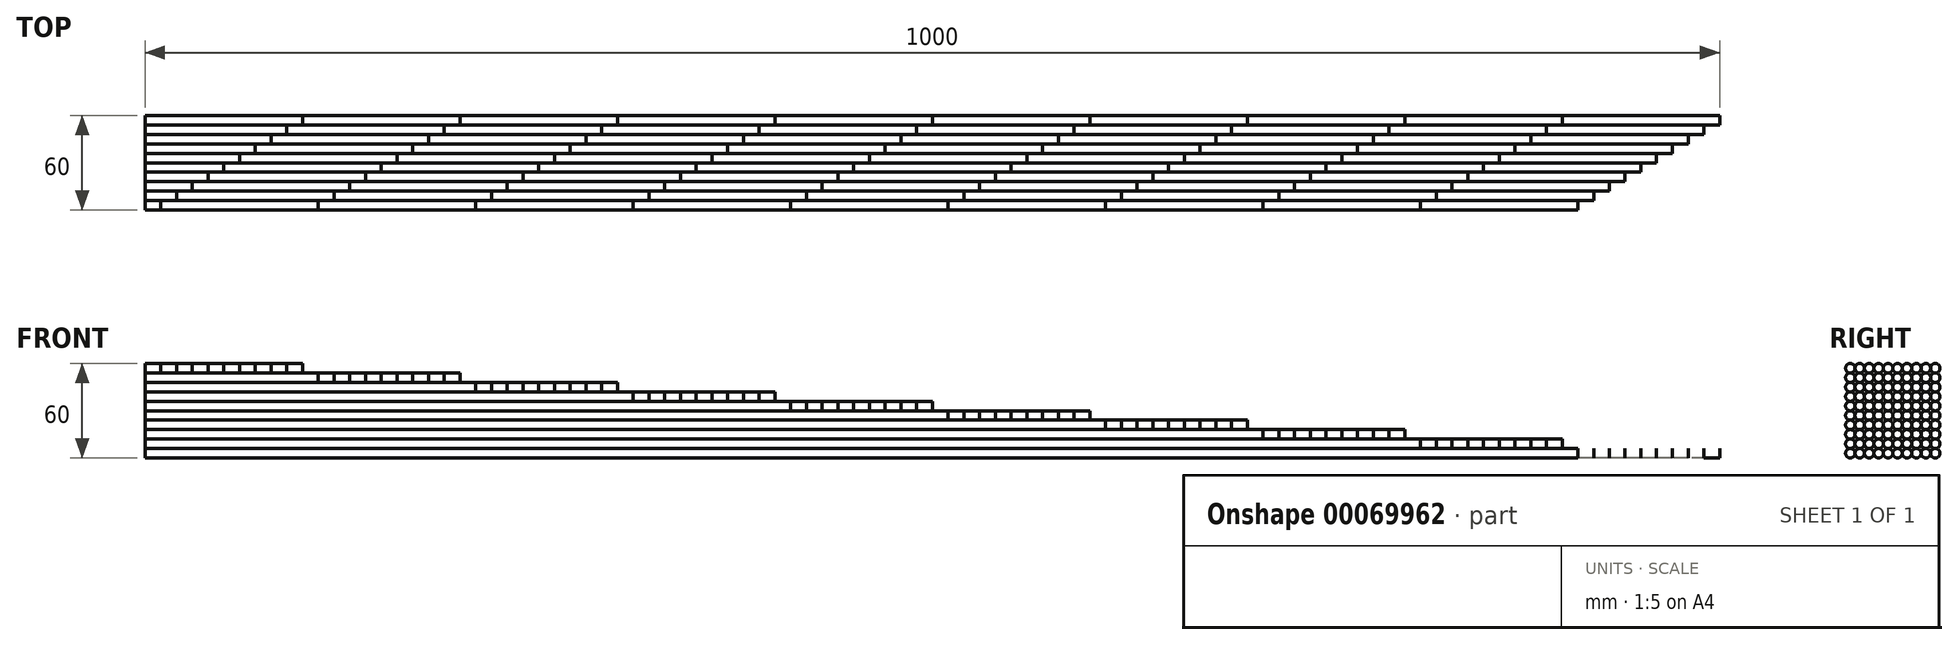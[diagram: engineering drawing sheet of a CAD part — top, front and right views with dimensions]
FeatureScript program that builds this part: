
annotation { "Feature Type Name" : "Feature", "Feature Type Description" : "" }
export const myFeature = defineFeature(function(context is Context, id is Id, definition is map)
    precondition{}
    {
        {
            var Q0;
            Q0=qCreatedBy(makeId("Right.planeOp"),FACE);
            var sketch = newSketch(context, id + "F0", { "sketchPlane" : qUnion([Q0])});
            skCircle(sketch, "E0", {"center": v(0, 0) * mm, "radius": 3 * mm});
            skCircle(sketch, "E1.0.1.0", {"center": v(0, 6) * mm, "radius": 3 * mm});
            skCircle(sketch, "E1.0.2.0", {"center": v(0, 12) * mm, "radius": 3 * mm});
            skCircle(sketch, "E1.0.3.0", {"center": v(0, 18) * mm, "radius": 3 * mm});
            skCircle(sketch, "E1.0.4.0", {"center": v(0, 24) * mm, "radius": 3 * mm});
            skCircle(sketch, "E1.0.5.0", {"center": v(0, 30) * mm, "radius": 3 * mm});
            skCircle(sketch, "E1.0.6.0", {"center": v(0, 36) * mm, "radius": 3 * mm});
            skCircle(sketch, "E1.0.7.0", {"center": v(0, 42) * mm, "radius": 3 * mm});
            skCircle(sketch, "E1.0.8.0", {"center": v(0, 48) * mm, "radius": 3 * mm});
            skCircle(sketch, "E1.0.9.0", {"center": v(0, 54) * mm, "radius": 3 * mm});
            skCircle(sketch, "E1.1.0.0", {"center": v(6, 0) * mm, "radius": 3 * mm});
            skCircle(sketch, "E1.1.1.0", {"center": v(6, 6) * mm, "radius": 3 * mm});
            skCircle(sketch, "E1.1.2.0", {"center": v(6, 12) * mm, "radius": 3 * mm});
            skCircle(sketch, "E1.1.3.0", {"center": v(6, 18) * mm, "radius": 3 * mm});
            skCircle(sketch, "E1.1.4.0", {"center": v(6, 24) * mm, "radius": 3 * mm});
            skCircle(sketch, "E1.1.5.0", {"center": v(6, 30) * mm, "radius": 3 * mm});
            skCircle(sketch, "E1.1.6.0", {"center": v(6, 36) * mm, "radius": 3 * mm});
            skCircle(sketch, "E1.1.7.0", {"center": v(6, 42) * mm, "radius": 3 * mm});
            skCircle(sketch, "E1.1.8.0", {"center": v(6, 48) * mm, "radius": 3 * mm});
            skCircle(sketch, "E1.1.9.0", {"center": v(6, 54) * mm, "radius": 3 * mm});
            skCircle(sketch, "E1.2.0.0", {"center": v(12, 0) * mm, "radius": 3 * mm});
            skCircle(sketch, "E1.2.1.0", {"center": v(12, 6) * mm, "radius": 3 * mm});
            skCircle(sketch, "E1.2.2.0", {"center": v(12, 12) * mm, "radius": 3 * mm});
            skCircle(sketch, "E1.2.3.0", {"center": v(12, 18) * mm, "radius": 3 * mm});
            skCircle(sketch, "E1.2.4.0", {"center": v(12, 24) * mm, "radius": 3 * mm});
            skCircle(sketch, "E1.2.5.0", {"center": v(12, 30) * mm, "radius": 3 * mm});
            skCircle(sketch, "E1.2.6.0", {"center": v(12, 36) * mm, "radius": 3 * mm});
            skCircle(sketch, "E1.2.7.0", {"center": v(12, 42) * mm, "radius": 3 * mm});
            skCircle(sketch, "E1.2.8.0", {"center": v(12, 48) * mm, "radius": 3 * mm});
            skCircle(sketch, "E1.2.9.0", {"center": v(12, 54) * mm, "radius": 3 * mm});
            skCircle(sketch, "E1.3.0.0", {"center": v(18, 0) * mm, "radius": 3 * mm});
            skCircle(sketch, "E1.3.1.0", {"center": v(18, 6) * mm, "radius": 3 * mm});
            skCircle(sketch, "E1.3.2.0", {"center": v(18, 12) * mm, "radius": 3 * mm});
            skCircle(sketch, "E1.3.3.0", {"center": v(18, 18) * mm, "radius": 3 * mm});
            skCircle(sketch, "E1.3.4.0", {"center": v(18, 24) * mm, "radius": 3 * mm});
            skCircle(sketch, "E1.3.5.0", {"center": v(18, 30) * mm, "radius": 3 * mm});
            skCircle(sketch, "E1.3.6.0", {"center": v(18, 36) * mm, "radius": 3 * mm});
            skCircle(sketch, "E1.3.7.0", {"center": v(18, 42) * mm, "radius": 3 * mm});
            skCircle(sketch, "E1.3.8.0", {"center": v(18, 48) * mm, "radius": 3 * mm});
            skCircle(sketch, "E1.3.9.0", {"center": v(18, 54) * mm, "radius": 3 * mm});
            skCircle(sketch, "E1.4.0.0", {"center": v(24, 0) * mm, "radius": 3 * mm});
            skCircle(sketch, "E1.4.1.0", {"center": v(24, 6) * mm, "radius": 3 * mm});
            skCircle(sketch, "E1.4.2.0", {"center": v(24, 12) * mm, "radius": 3 * mm});
            skCircle(sketch, "E1.4.3.0", {"center": v(24, 18) * mm, "radius": 3 * mm});
            skCircle(sketch, "E1.4.4.0", {"center": v(24, 24) * mm, "radius": 3 * mm});
            skCircle(sketch, "E1.4.5.0", {"center": v(24, 30) * mm, "radius": 3 * mm});
            skCircle(sketch, "E1.4.6.0", {"center": v(24, 36) * mm, "radius": 3 * mm});
            skCircle(sketch, "E1.4.7.0", {"center": v(24, 42) * mm, "radius": 3 * mm});
            skCircle(sketch, "E1.4.8.0", {"center": v(24, 48) * mm, "radius": 3 * mm});
            skCircle(sketch, "E1.4.9.0", {"center": v(24, 54) * mm, "radius": 3 * mm});
            skCircle(sketch, "E1.5.0.0", {"center": v(30, 0) * mm, "radius": 3 * mm});
            skCircle(sketch, "E1.5.1.0", {"center": v(30, 6) * mm, "radius": 3 * mm});
            skCircle(sketch, "E1.5.2.0", {"center": v(30, 12) * mm, "radius": 3 * mm});
            skCircle(sketch, "E1.5.3.0", {"center": v(30, 18) * mm, "radius": 3 * mm});
            skCircle(sketch, "E1.5.4.0", {"center": v(30, 24) * mm, "radius": 3 * mm});
            skCircle(sketch, "E1.5.5.0", {"center": v(30, 30) * mm, "radius": 3 * mm});
            skCircle(sketch, "E1.5.6.0", {"center": v(30, 36) * mm, "radius": 3 * mm});
            skCircle(sketch, "E1.5.7.0", {"center": v(30, 42) * mm, "radius": 3 * mm});
            skCircle(sketch, "E1.5.8.0", {"center": v(30, 48) * mm, "radius": 3 * mm});
            skCircle(sketch, "E1.5.9.0", {"center": v(30, 54) * mm, "radius": 3 * mm});
            skCircle(sketch, "E1.6.0.0", {"center": v(36, 0) * mm, "radius": 3 * mm});
            skCircle(sketch, "E1.6.1.0", {"center": v(36, 6) * mm, "radius": 3 * mm});
            skCircle(sketch, "E1.6.2.0", {"center": v(36, 12) * mm, "radius": 3 * mm});
            skCircle(sketch, "E1.6.3.0", {"center": v(36, 18) * mm, "radius": 3 * mm});
            skCircle(sketch, "E1.6.4.0", {"center": v(36, 24) * mm, "radius": 3 * mm});
            skCircle(sketch, "E1.6.5.0", {"center": v(36, 30) * mm, "radius": 3 * mm});
            skCircle(sketch, "E1.6.6.0", {"center": v(36, 36) * mm, "radius": 3 * mm});
            skCircle(sketch, "E1.6.7.0", {"center": v(36, 42) * mm, "radius": 3 * mm});
            skCircle(sketch, "E1.6.8.0", {"center": v(36, 48) * mm, "radius": 3 * mm});
            skCircle(sketch, "E1.6.9.0", {"center": v(36, 54) * mm, "radius": 3 * mm});
            skCircle(sketch, "E1.7.0.0", {"center": v(42, 0) * mm, "radius": 3 * mm});
            skCircle(sketch, "E1.7.1.0", {"center": v(42, 6) * mm, "radius": 3 * mm});
            skCircle(sketch, "E1.7.2.0", {"center": v(42, 12) * mm, "radius": 3 * mm});
            skCircle(sketch, "E1.7.3.0", {"center": v(42, 18) * mm, "radius": 3 * mm});
            skCircle(sketch, "E1.7.4.0", {"center": v(42, 24) * mm, "radius": 3 * mm});
            skCircle(sketch, "E1.7.5.0", {"center": v(42, 30) * mm, "radius": 3 * mm});
            skCircle(sketch, "E1.7.6.0", {"center": v(42, 36) * mm, "radius": 3 * mm});
            skCircle(sketch, "E1.7.7.0", {"center": v(42, 42) * mm, "radius": 3 * mm});
            skCircle(sketch, "E1.7.8.0", {"center": v(42, 48) * mm, "radius": 3 * mm});
            skCircle(sketch, "E1.7.9.0", {"center": v(42, 54) * mm, "radius": 3 * mm});
            skCircle(sketch, "E1.8.0.0", {"center": v(48, 0) * mm, "radius": 3 * mm});
            skCircle(sketch, "E1.8.1.0", {"center": v(48, 6) * mm, "radius": 3 * mm});
            skCircle(sketch, "E1.8.2.0", {"center": v(48, 12) * mm, "radius": 3 * mm});
            skCircle(sketch, "E1.8.3.0", {"center": v(48, 18) * mm, "radius": 3 * mm});
            skCircle(sketch, "E1.8.4.0", {"center": v(48, 24) * mm, "radius": 3 * mm});
            skCircle(sketch, "E1.8.5.0", {"center": v(48, 30) * mm, "radius": 3 * mm});
            skCircle(sketch, "E1.8.6.0", {"center": v(48, 36) * mm, "radius": 3 * mm});
            skCircle(sketch, "E1.8.7.0", {"center": v(48, 42) * mm, "radius": 3 * mm});
            skCircle(sketch, "E1.8.8.0", {"center": v(48, 48) * mm, "radius": 3 * mm});
            skCircle(sketch, "E1.8.9.0", {"center": v(48, 54) * mm, "radius": 3 * mm});
            skCircle(sketch, "E1.9.0.0", {"center": v(54, 0) * mm, "radius": 3 * mm});
            skCircle(sketch, "E1.9.1.0", {"center": v(54, 6) * mm, "radius": 3 * mm});
            skCircle(sketch, "E1.9.2.0", {"center": v(54, 12) * mm, "radius": 3 * mm});
            skCircle(sketch, "E1.9.3.0", {"center": v(54, 18) * mm, "radius": 3 * mm});
            skCircle(sketch, "E1.9.4.0", {"center": v(54, 24) * mm, "radius": 3 * mm});
            skCircle(sketch, "E1.9.5.0", {"center": v(54, 30) * mm, "radius": 3 * mm});
            skCircle(sketch, "E1.9.6.0", {"center": v(54, 36) * mm, "radius": 3 * mm});
            skCircle(sketch, "E1.9.7.0", {"center": v(54, 42) * mm, "radius": 3 * mm});
            skCircle(sketch, "E1.9.8.0", {"center": v(54, 48) * mm, "radius": 3 * mm});
            skCircle(sketch, "E1.9.9.0", {"center": v(54, 54) * mm, "radius": 3 * mm});
            skLineSegment(sketch, "E1.direction1", {"start": v(0, 0) * mm, "end": v(6, 0) * mm, "construction": true});
            skLineSegment(sketch, "E1.direction2", {"start": v(0, 0) * mm, "end": v(0, 6) * mm, "construction": true});
            skSolve(sketch);
        }
        {
            var Q0;
            {var subQ0=sQuery(id+"F0.wireOp",EDGE,"E1.0.9.0");var subQ1=makeQuery(id+"F0.imprint","INTERSECT",VERTEX,{"derivedFrom":[sQuery(id+"F0.wireOp",EDGE,"E1.0.8.0"),subQ0]});Q0=makeQuery(id+"F0.imprint","IMPRINT",FACE,{"disambiguationData":[TD([[makeQuery(id+"F0.imprint","IMPRINT",EDGE,{"disambiguationData":[TD([[subQ1,1.0]])],"derivedFrom":subQ0}),1.0]])]});}
            extrude(context, id + "F1", {"entities" : qUnion([Q0]), "depth" : 10 * mm});
        }
        {
            var Q0;
            {var subQ0=sQuery(id+"F0.wireOp",EDGE,"E1.1.9.0");var subQ1=makeQuery(id+"F0.imprint","INTERSECT",VERTEX,{"derivedFrom":[sQuery(id+"F0.wireOp",EDGE,"E1.0.9.0"),subQ0]});Q0=makeQuery(id+"F0.imprint","IMPRINT",FACE,{"disambiguationData":[TD([[makeQuery(id+"F0.imprint","IMPRINT",EDGE,{"disambiguationData":[TD([[subQ1,1.0]])],"derivedFrom":subQ0}),1.0]])]});}
            extrude(context, id + "F2", {"entities" : qUnion([Q0]), "depth" : 20 * mm});
        }
        {
            var Q0;
            {var subQ0=sQuery(id+"F0.wireOp",EDGE,"E1.2.9.0");var subQ1=makeQuery(id+"F0.imprint","INTERSECT",VERTEX,{"derivedFrom":[sQuery(id+"F0.wireOp",EDGE,"E1.1.9.0"),subQ0]});Q0=makeQuery(id+"F0.imprint","IMPRINT",FACE,{"disambiguationData":[TD([[makeQuery(id+"F0.imprint","IMPRINT",EDGE,{"disambiguationData":[TD([[subQ1,1.0]])],"derivedFrom":subQ0}),1.0]])]});}
            extrude(context, id + "F3", {"entities" : qUnion([Q0]), "depth" : 30 * mm});
        }
        {
            var Q0;
            {var subQ0=sQuery(id+"F0.wireOp",EDGE,"E1.3.9.0");var subQ1=makeQuery(id+"F0.imprint","INTERSECT",VERTEX,{"derivedFrom":[sQuery(id+"F0.wireOp",EDGE,"E1.2.9.0"),subQ0]});Q0=makeQuery(id+"F0.imprint","IMPRINT",FACE,{"disambiguationData":[TD([[makeQuery(id+"F0.imprint","IMPRINT",EDGE,{"disambiguationData":[TD([[subQ1,1.0]])],"derivedFrom":subQ0}),1.0]])]});}
            extrude(context, id + "F4", {"entities" : qUnion([Q0]), "depth" : 40 * mm});
        }
        {
            var Q0;
            {var subQ0=sQuery(id+"F0.wireOp",EDGE,"E1.4.9.0");var subQ1=makeQuery(id+"F0.imprint","INTERSECT",VERTEX,{"derivedFrom":[sQuery(id+"F0.wireOp",EDGE,"E1.3.9.0"),subQ0]});Q0=makeQuery(id+"F0.imprint","IMPRINT",FACE,{"disambiguationData":[TD([[makeQuery(id+"F0.imprint","IMPRINT",EDGE,{"disambiguationData":[TD([[subQ1,1.0]])],"derivedFrom":subQ0}),1.0]])]});}
            extrude(context, id + "F5", {"entities" : qUnion([Q0]), "depth" : 50 * mm});
        }
        {
            var Q0;
            {var subQ0=sQuery(id+"F0.wireOp",EDGE,"E1.5.9.0");var subQ1=makeQuery(id+"F0.imprint","INTERSECT",VERTEX,{"derivedFrom":[sQuery(id+"F0.wireOp",EDGE,"E1.4.9.0"),subQ0]});Q0=makeQuery(id+"F0.imprint","IMPRINT",FACE,{"disambiguationData":[TD([[makeQuery(id+"F0.imprint","IMPRINT",EDGE,{"disambiguationData":[TD([[subQ1,1.0]])],"derivedFrom":subQ0}),1.0]])]});}
            extrude(context, id + "F6", {"entities" : qUnion([Q0]), "depth" : 60 * mm});
        }
        {
            var Q0;
            {var subQ0=sQuery(id+"F0.wireOp",EDGE,"E1.6.9.0");var subQ1=makeQuery(id+"F0.imprint","INTERSECT",VERTEX,{"derivedFrom":[sQuery(id+"F0.wireOp",EDGE,"E1.5.9.0"),subQ0]});Q0=makeQuery(id+"F0.imprint","IMPRINT",FACE,{"disambiguationData":[TD([[makeQuery(id+"F0.imprint","IMPRINT",EDGE,{"disambiguationData":[TD([[subQ1,1.0]])],"derivedFrom":subQ0}),1.0]])]});}
            extrude(context, id + "F7", {"entities" : qUnion([Q0]), "depth" : 70 * mm});
        }
        {
            var Q0;
            {var subQ0=sQuery(id+"F0.wireOp",EDGE,"E1.7.9.0");var subQ1=makeQuery(id+"F0.imprint","INTERSECT",VERTEX,{"derivedFrom":[sQuery(id+"F0.wireOp",EDGE,"E1.6.9.0"),subQ0]});Q0=makeQuery(id+"F0.imprint","IMPRINT",FACE,{"disambiguationData":[TD([[makeQuery(id+"F0.imprint","IMPRINT",EDGE,{"disambiguationData":[TD([[subQ1,1.0]])],"derivedFrom":subQ0}),1.0]])]});}
            extrude(context, id + "F8", {"entities" : qUnion([Q0]), "depth" : 80 * mm});
        }
        {
            var Q0;
            {var subQ0=sQuery(id+"F0.wireOp",EDGE,"E1.8.9.0");var subQ1=makeQuery(id+"F0.imprint","INTERSECT",VERTEX,{"derivedFrom":[sQuery(id+"F0.wireOp",EDGE,"E1.7.9.0"),subQ0]});Q0=makeQuery(id+"F0.imprint","IMPRINT",FACE,{"disambiguationData":[TD([[makeQuery(id+"F0.imprint","IMPRINT",EDGE,{"disambiguationData":[TD([[subQ1,1.0]])],"derivedFrom":subQ0}),1.0]])]});}
            extrude(context, id + "F9", {"entities" : qUnion([Q0]), "depth" : 90 * mm});
        }
        {
            var Q0;
            {var subQ0=sQuery(id+"F0.wireOp",EDGE,"E1.9.9.0");var subQ1=makeQuery(id+"F0.imprint","INTERSECT",VERTEX,{"derivedFrom":[sQuery(id+"F0.wireOp",EDGE,"E1.8.9.0"),subQ0]});Q0=makeQuery(id+"F0.imprint","IMPRINT",FACE,{"disambiguationData":[TD([[makeQuery(id+"F0.imprint","IMPRINT",EDGE,{"disambiguationData":[TD([[subQ1,-1.0]])],"derivedFrom":subQ0}),1.0]])]});}
            extrude(context, id + "F10", {"entities" : qUnion([Q0]), "depth" : 100 * mm});
        }
        {
            var Q0;
            {var subQ0=sQuery(id+"F0.wireOp",EDGE,"E1.0.8.0");var subQ1=makeQuery(id+"F0.imprint","INTERSECT",VERTEX,{"derivedFrom":[subQ0,sQuery(id+"F0.wireOp",EDGE,"E1.0.9.0")]});Q0=makeQuery(id+"F0.imprint","IMPRINT",FACE,{"disambiguationData":[TD([[makeQuery(id+"F0.imprint","IMPRINT",EDGE,{"disambiguationData":[TD([[subQ1,1.0]])],"derivedFrom":subQ0}),1.0]])]});}
            extrude(context, id + "F11", {"entities" : qUnion([Q0]), "depth" : 110 * mm});
        }
        {
            var Q0;
            {var subQ0=sQuery(id+"F0.wireOp",EDGE,"E1.1.8.0");var subQ1=makeQuery(id+"F0.imprint","INTERSECT",VERTEX,{"derivedFrom":[subQ0,sQuery(id+"F0.wireOp",EDGE,"E1.1.9.0")]});Q0=makeQuery(id+"F0.imprint","IMPRINT",FACE,{"disambiguationData":[TD([[makeQuery(id+"F0.imprint","IMPRINT",EDGE,{"disambiguationData":[TD([[subQ1,1.0]])],"derivedFrom":subQ0}),1.0]])]});}
            extrude(context, id + "F12", {"entities" : qUnion([Q0]), "depth" : 120 * mm});
        }
        {
            var Q0;
            {var subQ0=sQuery(id+"F0.wireOp",EDGE,"E1.2.8.0");var subQ1=makeQuery(id+"F0.imprint","INTERSECT",VERTEX,{"derivedFrom":[subQ0,sQuery(id+"F0.wireOp",EDGE,"E1.2.9.0")]});Q0=makeQuery(id+"F0.imprint","IMPRINT",FACE,{"disambiguationData":[TD([[makeQuery(id+"F0.imprint","IMPRINT",EDGE,{"disambiguationData":[TD([[subQ1,1.0]])],"derivedFrom":subQ0}),1.0]])]});}
            extrude(context, id + "F13", {"entities" : qUnion([Q0]), "depth" : 130 * mm});
        }
        {
            var Q0;
            {var subQ0=sQuery(id+"F0.wireOp",EDGE,"E1.3.8.0");var subQ1=makeQuery(id+"F0.imprint","INTERSECT",VERTEX,{"derivedFrom":[subQ0,sQuery(id+"F0.wireOp",EDGE,"E1.3.9.0")]});Q0=makeQuery(id+"F0.imprint","IMPRINT",FACE,{"disambiguationData":[TD([[makeQuery(id+"F0.imprint","IMPRINT",EDGE,{"disambiguationData":[TD([[subQ1,1.0]])],"derivedFrom":subQ0}),1.0]])]});}
            extrude(context, id + "F14", {"entities" : qUnion([Q0]), "depth" : 140 * mm});
        }
        {
            var Q0;
            {var subQ0=sQuery(id+"F0.wireOp",EDGE,"E1.4.8.0");var subQ1=makeQuery(id+"F0.imprint","INTERSECT",VERTEX,{"derivedFrom":[subQ0,sQuery(id+"F0.wireOp",EDGE,"E1.4.9.0")]});Q0=makeQuery(id+"F0.imprint","IMPRINT",FACE,{"disambiguationData":[TD([[makeQuery(id+"F0.imprint","IMPRINT",EDGE,{"disambiguationData":[TD([[subQ1,1.0]])],"derivedFrom":subQ0}),1.0]])]});}
            extrude(context, id + "F15", {"entities" : qUnion([Q0]), "depth" : 150 * mm});
        }
        {
            var Q0;
            {var subQ0=sQuery(id+"F0.wireOp",EDGE,"E1.5.8.0");var subQ1=makeQuery(id+"F0.imprint","INTERSECT",VERTEX,{"derivedFrom":[subQ0,sQuery(id+"F0.wireOp",EDGE,"E1.5.9.0")]});Q0=makeQuery(id+"F0.imprint","IMPRINT",FACE,{"disambiguationData":[TD([[makeQuery(id+"F0.imprint","IMPRINT",EDGE,{"disambiguationData":[TD([[subQ1,1.0]])],"derivedFrom":subQ0}),1.0]])]});}
            extrude(context, id + "F16", {"entities" : qUnion([Q0]), "depth" : 160 * mm});
        }
        {
            var Q0;
            {var subQ0=sQuery(id+"F0.wireOp",EDGE,"E1.6.8.0");var subQ1=makeQuery(id+"F0.imprint","INTERSECT",VERTEX,{"derivedFrom":[subQ0,sQuery(id+"F0.wireOp",EDGE,"E1.6.9.0")]});Q0=makeQuery(id+"F0.imprint","IMPRINT",FACE,{"disambiguationData":[TD([[makeQuery(id+"F0.imprint","IMPRINT",EDGE,{"disambiguationData":[TD([[subQ1,1.0]])],"derivedFrom":subQ0}),1.0]])]});}
            extrude(context, id + "F17", {"entities" : qUnion([Q0]), "depth" : 170 * mm});
        }
        {
            var Q0;
            {var subQ0=sQuery(id+"F0.wireOp",EDGE,"E1.7.8.0");var subQ1=makeQuery(id+"F0.imprint","INTERSECT",VERTEX,{"derivedFrom":[subQ0,sQuery(id+"F0.wireOp",EDGE,"E1.7.9.0")]});Q0=makeQuery(id+"F0.imprint","IMPRINT",FACE,{"disambiguationData":[TD([[makeQuery(id+"F0.imprint","IMPRINT",EDGE,{"disambiguationData":[TD([[subQ1,1.0]])],"derivedFrom":subQ0}),1.0]])]});}
            extrude(context, id + "F18", {"entities" : qUnion([Q0]), "depth" : 180 * mm});
        }
        {
            var Q0;
            {var subQ0=sQuery(id+"F0.wireOp",EDGE,"E1.8.8.0");var subQ1=makeQuery(id+"F0.imprint","INTERSECT",VERTEX,{"derivedFrom":[subQ0,sQuery(id+"F0.wireOp",EDGE,"E1.8.9.0")]});Q0=makeQuery(id+"F0.imprint","IMPRINT",FACE,{"disambiguationData":[TD([[makeQuery(id+"F0.imprint","IMPRINT",EDGE,{"disambiguationData":[TD([[subQ1,1.0]])],"derivedFrom":subQ0}),1.0]])]});}
            extrude(context, id + "F19", {"entities" : qUnion([Q0]), "depth" : 190 * mm});
        }
        {
            var Q0;
            {var subQ0=sQuery(id+"F0.wireOp",EDGE,"E1.9.8.0");var subQ1=makeQuery(id+"F0.imprint","INTERSECT",VERTEX,{"derivedFrom":[subQ0,sQuery(id+"F0.wireOp",EDGE,"E1.9.9.0")]});Q0=makeQuery(id+"F0.imprint","IMPRINT",FACE,{"disambiguationData":[TD([[makeQuery(id+"F0.imprint","IMPRINT",EDGE,{"disambiguationData":[TD([[subQ1,-1.0]])],"derivedFrom":subQ0}),1.0]])]});}
            extrude(context, id + "F20", {"entities" : qUnion([Q0]), "depth" : 200 * mm});
        }
        {
            var Q0;
            {var subQ0=sQuery(id+"F0.wireOp",EDGE,"E1.0.7.0");var subQ1=makeQuery(id+"F0.imprint","INTERSECT",VERTEX,{"derivedFrom":[subQ0,sQuery(id+"F0.wireOp",EDGE,"E1.0.8.0")]});Q0=makeQuery(id+"F0.imprint","IMPRINT",FACE,{"disambiguationData":[TD([[makeQuery(id+"F0.imprint","IMPRINT",EDGE,{"disambiguationData":[TD([[subQ1,1.0]])],"derivedFrom":subQ0}),1.0]])]});}
            extrude(context, id + "F21", {"entities" : qUnion([Q0]), "depth" : 210 * mm});
        }
        {
            var Q0;
            {var subQ0=sQuery(id+"F0.wireOp",EDGE,"E1.1.7.0");var subQ1=makeQuery(id+"F0.imprint","INTERSECT",VERTEX,{"derivedFrom":[subQ0,sQuery(id+"F0.wireOp",EDGE,"E1.1.8.0")]});Q0=makeQuery(id+"F0.imprint","IMPRINT",FACE,{"disambiguationData":[TD([[makeQuery(id+"F0.imprint","IMPRINT",EDGE,{"disambiguationData":[TD([[subQ1,1.0]])],"derivedFrom":subQ0}),1.0]])]});}
            extrude(context, id + "F22", {"entities" : qUnion([Q0]), "depth" : 220 * mm});
        }
        {
            var Q0;
            {var subQ0=sQuery(id+"F0.wireOp",EDGE,"E1.2.7.0");var subQ1=makeQuery(id+"F0.imprint","INTERSECT",VERTEX,{"derivedFrom":[subQ0,sQuery(id+"F0.wireOp",EDGE,"E1.2.8.0")]});Q0=makeQuery(id+"F0.imprint","IMPRINT",FACE,{"disambiguationData":[TD([[makeQuery(id+"F0.imprint","IMPRINT",EDGE,{"disambiguationData":[TD([[subQ1,1.0]])],"derivedFrom":subQ0}),1.0]])]});}
            extrude(context, id + "F23", {"entities" : qUnion([Q0]), "depth" : 230 * mm});
        }
        {
            var Q0;
            {var subQ0=sQuery(id+"F0.wireOp",EDGE,"E1.3.7.0");var subQ1=makeQuery(id+"F0.imprint","INTERSECT",VERTEX,{"derivedFrom":[subQ0,sQuery(id+"F0.wireOp",EDGE,"E1.3.8.0")]});Q0=makeQuery(id+"F0.imprint","IMPRINT",FACE,{"disambiguationData":[TD([[makeQuery(id+"F0.imprint","IMPRINT",EDGE,{"disambiguationData":[TD([[subQ1,1.0]])],"derivedFrom":subQ0}),1.0]])]});}
            var Q1;
            Q1=sQuery(id+"F0.wireOp",EDGE,"E1.3.7.0");
            extrude(context, id + "F24", {"entities" : qUnion([Q0]), "surfaceEntities" : qUnion([Q1]), "depth" : 240 * mm});
        }
        {
            var Q0;
            {var subQ0=sQuery(id+"F0.wireOp",EDGE,"E1.4.7.0");var subQ1=makeQuery(id+"F0.imprint","INTERSECT",VERTEX,{"derivedFrom":[subQ0,sQuery(id+"F0.wireOp",EDGE,"E1.4.8.0")]});Q0=makeQuery(id+"F0.imprint","IMPRINT",FACE,{"disambiguationData":[TD([[makeQuery(id+"F0.imprint","IMPRINT",EDGE,{"disambiguationData":[TD([[subQ1,1.0]])],"derivedFrom":subQ0}),1.0]])]});}
            extrude(context, id + "F25", {"entities" : qUnion([Q0]), "depth" : 250 * mm});
        }
        {
            var Q0;
            {var subQ0=sQuery(id+"F0.wireOp",EDGE,"E1.5.7.0");var subQ1=makeQuery(id+"F0.imprint","INTERSECT",VERTEX,{"derivedFrom":[subQ0,sQuery(id+"F0.wireOp",EDGE,"E1.5.8.0")]});Q0=makeQuery(id+"F0.imprint","IMPRINT",FACE,{"disambiguationData":[TD([[makeQuery(id+"F0.imprint","IMPRINT",EDGE,{"disambiguationData":[TD([[subQ1,1.0]])],"derivedFrom":subQ0}),1.0]])]});}
            extrude(context, id + "F26", {"entities" : qUnion([Q0]), "depth" : 260 * mm});
        }
        {
            var Q0;
            {var subQ0=sQuery(id+"F0.wireOp",EDGE,"E1.6.7.0");var subQ1=makeQuery(id+"F0.imprint","INTERSECT",VERTEX,{"derivedFrom":[subQ0,sQuery(id+"F0.wireOp",EDGE,"E1.6.8.0")]});Q0=makeQuery(id+"F0.imprint","IMPRINT",FACE,{"disambiguationData":[TD([[makeQuery(id+"F0.imprint","IMPRINT",EDGE,{"disambiguationData":[TD([[subQ1,1.0]])],"derivedFrom":subQ0}),1.0]])]});}
            extrude(context, id + "F27", {"entities" : qUnion([Q0]), "depth" : 270 * mm});
        }
        {
            var Q0;
            {var subQ0=sQuery(id+"F0.wireOp",EDGE,"E1.7.7.0");var subQ1=makeQuery(id+"F0.imprint","INTERSECT",VERTEX,{"derivedFrom":[subQ0,sQuery(id+"F0.wireOp",EDGE,"E1.7.8.0")]});Q0=makeQuery(id+"F0.imprint","IMPRINT",FACE,{"disambiguationData":[TD([[makeQuery(id+"F0.imprint","IMPRINT",EDGE,{"disambiguationData":[TD([[subQ1,1.0]])],"derivedFrom":subQ0}),1.0]])]});}
            extrude(context, id + "F28", {"entities" : qUnion([Q0]), "depth" : 280 * mm});
        }
        {
            var Q0;
            {var subQ0=sQuery(id+"F0.wireOp",EDGE,"E1.8.7.0");var subQ1=makeQuery(id+"F0.imprint","INTERSECT",VERTEX,{"derivedFrom":[subQ0,sQuery(id+"F0.wireOp",EDGE,"E1.8.8.0")]});Q0=makeQuery(id+"F0.imprint","IMPRINT",FACE,{"disambiguationData":[TD([[makeQuery(id+"F0.imprint","IMPRINT",EDGE,{"disambiguationData":[TD([[subQ1,1.0]])],"derivedFrom":subQ0}),1.0]])]});}
            extrude(context, id + "F29", {"entities" : qUnion([Q0]), "depth" : 290 * mm});
        }
        {
            var Q0;
            {var subQ0=sQuery(id+"F0.wireOp",EDGE,"E1.9.7.0");var subQ1=makeQuery(id+"F0.imprint","INTERSECT",VERTEX,{"derivedFrom":[subQ0,sQuery(id+"F0.wireOp",EDGE,"E1.9.8.0")]});Q0=makeQuery(id+"F0.imprint","IMPRINT",FACE,{"disambiguationData":[TD([[makeQuery(id+"F0.imprint","IMPRINT",EDGE,{"disambiguationData":[TD([[subQ1,-1.0]])],"derivedFrom":subQ0}),1.0]])]});}
            extrude(context, id + "F30", {"entities" : qUnion([Q0]), "depth" : 300 * mm});
        }
        {
            var Q0;
            {var subQ0=sQuery(id+"F0.wireOp",EDGE,"E1.0.6.0");var subQ1=makeQuery(id+"F0.imprint","INTERSECT",VERTEX,{"derivedFrom":[subQ0,sQuery(id+"F0.wireOp",EDGE,"E1.0.7.0")]});Q0=makeQuery(id+"F0.imprint","IMPRINT",FACE,{"disambiguationData":[TD([[makeQuery(id+"F0.imprint","IMPRINT",EDGE,{"disambiguationData":[TD([[subQ1,1.0]])],"derivedFrom":subQ0}),1.0]])]});}
            extrude(context, id + "F31", {"entities" : qUnion([Q0]), "depth" : 310 * mm});
        }
        {
            var Q0;
            {var subQ0=sQuery(id+"F0.wireOp",EDGE,"E1.1.6.0");var subQ1=makeQuery(id+"F0.imprint","INTERSECT",VERTEX,{"derivedFrom":[subQ0,sQuery(id+"F0.wireOp",EDGE,"E1.1.7.0")]});Q0=makeQuery(id+"F0.imprint","IMPRINT",FACE,{"disambiguationData":[TD([[makeQuery(id+"F0.imprint","IMPRINT",EDGE,{"disambiguationData":[TD([[subQ1,1.0]])],"derivedFrom":subQ0}),1.0]])]});}
            extrude(context, id + "F32", {"entities" : qUnion([Q0]), "depth" : 320 * mm});
        }
        {
            var Q0;
            {var subQ0=sQuery(id+"F0.wireOp",EDGE,"E1.2.6.0");var subQ1=makeQuery(id+"F0.imprint","INTERSECT",VERTEX,{"derivedFrom":[subQ0,sQuery(id+"F0.wireOp",EDGE,"E1.2.7.0")]});Q0=makeQuery(id+"F0.imprint","IMPRINT",FACE,{"disambiguationData":[TD([[makeQuery(id+"F0.imprint","IMPRINT",EDGE,{"disambiguationData":[TD([[subQ1,1.0]])],"derivedFrom":subQ0}),1.0]])]});}
            extrude(context, id + "F33", {"entities" : qUnion([Q0]), "depth" : 330 * mm});
        }
        {
            var Q0;
            {var subQ0=sQuery(id+"F0.wireOp",EDGE,"E1.3.6.0");var subQ1=makeQuery(id+"F0.imprint","INTERSECT",VERTEX,{"derivedFrom":[subQ0,sQuery(id+"F0.wireOp",EDGE,"E1.3.7.0")]});Q0=makeQuery(id+"F0.imprint","IMPRINT",FACE,{"disambiguationData":[TD([[makeQuery(id+"F0.imprint","IMPRINT",EDGE,{"disambiguationData":[TD([[subQ1,1.0]])],"derivedFrom":subQ0}),1.0]])]});}
            extrude(context, id + "F34", {"entities" : qUnion([Q0]), "depth" : 340 * mm});
        }
        {
            var Q0;
            {var subQ0=sQuery(id+"F0.wireOp",EDGE,"E1.4.6.0");var subQ1=makeQuery(id+"F0.imprint","INTERSECT",VERTEX,{"derivedFrom":[subQ0,sQuery(id+"F0.wireOp",EDGE,"E1.4.7.0")]});Q0=makeQuery(id+"F0.imprint","IMPRINT",FACE,{"disambiguationData":[TD([[makeQuery(id+"F0.imprint","IMPRINT",EDGE,{"disambiguationData":[TD([[subQ1,1.0]])],"derivedFrom":subQ0}),1.0]])]});}
            extrude(context, id + "F35", {"entities" : qUnion([Q0]), "depth" : 350 * mm});
        }
        {
            var Q0;
            {var subQ0=sQuery(id+"F0.wireOp",EDGE,"E1.5.6.0");var subQ1=makeQuery(id+"F0.imprint","INTERSECT",VERTEX,{"derivedFrom":[subQ0,sQuery(id+"F0.wireOp",EDGE,"E1.5.7.0")]});Q0=makeQuery(id+"F0.imprint","IMPRINT",FACE,{"disambiguationData":[TD([[makeQuery(id+"F0.imprint","IMPRINT",EDGE,{"disambiguationData":[TD([[subQ1,1.0]])],"derivedFrom":subQ0}),1.0]])]});}
            extrude(context, id + "F36", {"entities" : qUnion([Q0]), "depth" : 360 * mm});
        }
        {
            var Q0;
            {var subQ0=sQuery(id+"F0.wireOp",EDGE,"E1.6.6.0");var subQ1=makeQuery(id+"F0.imprint","INTERSECT",VERTEX,{"derivedFrom":[subQ0,sQuery(id+"F0.wireOp",EDGE,"E1.6.7.0")]});Q0=makeQuery(id+"F0.imprint","IMPRINT",FACE,{"disambiguationData":[TD([[makeQuery(id+"F0.imprint","IMPRINT",EDGE,{"disambiguationData":[TD([[subQ1,1.0]])],"derivedFrom":subQ0}),1.0]])]});}
            extrude(context, id + "F37", {"entities" : qUnion([Q0]), "depth" : 370 * mm});
        }
        {
            var Q0;
            {var subQ0=sQuery(id+"F0.wireOp",EDGE,"E1.7.6.0");var subQ1=makeQuery(id+"F0.imprint","INTERSECT",VERTEX,{"derivedFrom":[subQ0,sQuery(id+"F0.wireOp",EDGE,"E1.7.7.0")]});Q0=makeQuery(id+"F0.imprint","IMPRINT",FACE,{"disambiguationData":[TD([[makeQuery(id+"F0.imprint","IMPRINT",EDGE,{"disambiguationData":[TD([[subQ1,1.0]])],"derivedFrom":subQ0}),1.0]])]});}
            var Q1;
            Q1=sQuery(id+"F0.wireOp",EDGE,"E1.7.6.0");
            extrude(context, id + "F38", {"entities" : qUnion([Q0]), "surfaceEntities" : qUnion([Q1]), "depth" : 380 * mm});
        }
        {
            var Q0;
            {var subQ0=sQuery(id+"F0.wireOp",EDGE,"E1.8.6.0");var subQ1=makeQuery(id+"F0.imprint","INTERSECT",VERTEX,{"derivedFrom":[subQ0,sQuery(id+"F0.wireOp",EDGE,"E1.8.7.0")]});Q0=makeQuery(id+"F0.imprint","IMPRINT",FACE,{"disambiguationData":[TD([[makeQuery(id+"F0.imprint","IMPRINT",EDGE,{"disambiguationData":[TD([[subQ1,1.0]])],"derivedFrom":subQ0}),1.0]])]});}
            extrude(context, id + "F39", {"entities" : qUnion([Q0]), "depth" : 390 * mm});
        }
        {
            var Q0;
            {var subQ0=sQuery(id+"F0.wireOp",EDGE,"E1.9.6.0");var subQ1=makeQuery(id+"F0.imprint","INTERSECT",VERTEX,{"derivedFrom":[subQ0,sQuery(id+"F0.wireOp",EDGE,"E1.9.7.0")]});Q0=makeQuery(id+"F0.imprint","IMPRINT",FACE,{"disambiguationData":[TD([[makeQuery(id+"F0.imprint","IMPRINT",EDGE,{"disambiguationData":[TD([[subQ1,-1.0]])],"derivedFrom":subQ0}),1.0]])]});}
            extrude(context, id + "F40", {"entities" : qUnion([Q0]), "depth" : 400 * mm});
        }
        {
            var Q0;
            {var subQ0=sQuery(id+"F0.wireOp",EDGE,"E1.0.5.0");var subQ1=makeQuery(id+"F0.imprint","INTERSECT",VERTEX,{"derivedFrom":[subQ0,sQuery(id+"F0.wireOp",EDGE,"E1.0.6.0")]});Q0=makeQuery(id+"F0.imprint","IMPRINT",FACE,{"disambiguationData":[TD([[makeQuery(id+"F0.imprint","IMPRINT",EDGE,{"disambiguationData":[TD([[subQ1,1.0]])],"derivedFrom":subQ0}),1.0]])]});}
            extrude(context, id + "F41", {"entities" : qUnion([Q0]), "depth" : 410 * mm});
        }
        {
            var Q0;
            {var subQ0=sQuery(id+"F0.wireOp",EDGE,"E1.1.5.0");var subQ1=makeQuery(id+"F0.imprint","INTERSECT",VERTEX,{"derivedFrom":[subQ0,sQuery(id+"F0.wireOp",EDGE,"E1.1.6.0")]});Q0=makeQuery(id+"F0.imprint","IMPRINT",FACE,{"disambiguationData":[TD([[makeQuery(id+"F0.imprint","IMPRINT",EDGE,{"disambiguationData":[TD([[subQ1,1.0]])],"derivedFrom":subQ0}),1.0]])]});}
            extrude(context, id + "F42", {"entities" : qUnion([Q0]), "depth" : 420 * mm});
        }
        {
            var Q0;
            {var subQ0=sQuery(id+"F0.wireOp",EDGE,"E1.2.5.0");var subQ1=makeQuery(id+"F0.imprint","INTERSECT",VERTEX,{"derivedFrom":[subQ0,sQuery(id+"F0.wireOp",EDGE,"E1.2.6.0")]});Q0=makeQuery(id+"F0.imprint","IMPRINT",FACE,{"disambiguationData":[TD([[makeQuery(id+"F0.imprint","IMPRINT",EDGE,{"disambiguationData":[TD([[subQ1,1.0]])],"derivedFrom":subQ0}),1.0]])]});}
            extrude(context, id + "F43", {"entities" : qUnion([Q0]), "depth" : 430 * mm});
        }
        {
            var Q0;
            {var subQ0=sQuery(id+"F0.wireOp",EDGE,"E1.3.5.0");var subQ1=makeQuery(id+"F0.imprint","INTERSECT",VERTEX,{"derivedFrom":[subQ0,sQuery(id+"F0.wireOp",EDGE,"E1.3.6.0")]});Q0=makeQuery(id+"F0.imprint","IMPRINT",FACE,{"disambiguationData":[TD([[makeQuery(id+"F0.imprint","IMPRINT",EDGE,{"disambiguationData":[TD([[subQ1,1.0]])],"derivedFrom":subQ0}),1.0]])]});}
            extrude(context, id + "F44", {"entities" : qUnion([Q0]), "depth" : 440 * mm});
        }
        {
            var Q0;
            {var subQ0=sQuery(id+"F0.wireOp",EDGE,"E1.4.5.0");var subQ1=makeQuery(id+"F0.imprint","INTERSECT",VERTEX,{"derivedFrom":[subQ0,sQuery(id+"F0.wireOp",EDGE,"E1.4.6.0")]});Q0=makeQuery(id+"F0.imprint","IMPRINT",FACE,{"disambiguationData":[TD([[makeQuery(id+"F0.imprint","IMPRINT",EDGE,{"disambiguationData":[TD([[subQ1,1.0]])],"derivedFrom":subQ0}),1.0]])]});}
            extrude(context, id + "F45", {"entities" : qUnion([Q0]), "depth" : 450 * mm});
        }
        {
            var Q0;
            {var subQ0=sQuery(id+"F0.wireOp",EDGE,"E1.5.5.0");var subQ1=makeQuery(id+"F0.imprint","INTERSECT",VERTEX,{"derivedFrom":[subQ0,sQuery(id+"F0.wireOp",EDGE,"E1.5.6.0")]});Q0=makeQuery(id+"F0.imprint","IMPRINT",FACE,{"disambiguationData":[TD([[makeQuery(id+"F0.imprint","IMPRINT",EDGE,{"disambiguationData":[TD([[subQ1,1.0]])],"derivedFrom":subQ0}),1.0]])]});}
            extrude(context, id + "F46", {"entities" : qUnion([Q0]), "depth" : 460 * mm});
        }
        {
            var Q0;
            {var subQ0=sQuery(id+"F0.wireOp",EDGE,"E1.6.5.0");var subQ1=makeQuery(id+"F0.imprint","INTERSECT",VERTEX,{"derivedFrom":[subQ0,sQuery(id+"F0.wireOp",EDGE,"E1.6.6.0")]});Q0=makeQuery(id+"F0.imprint","IMPRINT",FACE,{"disambiguationData":[TD([[makeQuery(id+"F0.imprint","IMPRINT",EDGE,{"disambiguationData":[TD([[subQ1,1.0]])],"derivedFrom":subQ0}),1.0]])]});}
            extrude(context, id + "F47", {"entities" : qUnion([Q0]), "depth" : 470 * mm});
        }
        {
            var Q0;
            {var subQ0=sQuery(id+"F0.wireOp",EDGE,"E1.7.5.0");var subQ1=makeQuery(id+"F0.imprint","INTERSECT",VERTEX,{"derivedFrom":[subQ0,sQuery(id+"F0.wireOp",EDGE,"E1.7.6.0")]});Q0=makeQuery(id+"F0.imprint","IMPRINT",FACE,{"disambiguationData":[TD([[makeQuery(id+"F0.imprint","IMPRINT",EDGE,{"disambiguationData":[TD([[subQ1,1.0]])],"derivedFrom":subQ0}),1.0]])]});}
            extrude(context, id + "F48", {"entities" : qUnion([Q0]), "depth" : 480 * mm});
        }
        {
            var Q0;
            {var subQ0=sQuery(id+"F0.wireOp",EDGE,"E1.8.5.0");var subQ1=makeQuery(id+"F0.imprint","INTERSECT",VERTEX,{"derivedFrom":[subQ0,sQuery(id+"F0.wireOp",EDGE,"E1.8.6.0")]});Q0=makeQuery(id+"F0.imprint","IMPRINT",FACE,{"disambiguationData":[TD([[makeQuery(id+"F0.imprint","IMPRINT",EDGE,{"disambiguationData":[TD([[subQ1,1.0]])],"derivedFrom":subQ0}),1.0]])]});}
            extrude(context, id + "F49", {"entities" : qUnion([Q0]), "depth" : 490 * mm});
        }
        {
            var Q0;
            {var subQ0=sQuery(id+"F0.wireOp",EDGE,"E1.9.5.0");var subQ1=makeQuery(id+"F0.imprint","INTERSECT",VERTEX,{"derivedFrom":[subQ0,sQuery(id+"F0.wireOp",EDGE,"E1.9.6.0")]});Q0=makeQuery(id+"F0.imprint","IMPRINT",FACE,{"disambiguationData":[TD([[makeQuery(id+"F0.imprint","IMPRINT",EDGE,{"disambiguationData":[TD([[subQ1,-1.0]])],"derivedFrom":subQ0}),1.0]])]});}
            extrude(context, id + "F50", {"entities" : qUnion([Q0]), "depth" : 500 * mm});
        }
        {
            var Q0;
            {var subQ0=sQuery(id+"F0.wireOp",EDGE,"E1.0.4.0");var subQ1=makeQuery(id+"F0.imprint","INTERSECT",VERTEX,{"derivedFrom":[subQ0,sQuery(id+"F0.wireOp",EDGE,"E1.0.5.0")]});Q0=makeQuery(id+"F0.imprint","IMPRINT",FACE,{"disambiguationData":[TD([[makeQuery(id+"F0.imprint","IMPRINT",EDGE,{"disambiguationData":[TD([[subQ1,1.0]])],"derivedFrom":subQ0}),1.0]])]});}
            extrude(context, id + "F51", {"entities" : qUnion([Q0]), "depth" : 510 * mm});
        }
        {
            var Q0;
            {var subQ0=sQuery(id+"F0.wireOp",EDGE,"E1.1.4.0");var subQ1=makeQuery(id+"F0.imprint","INTERSECT",VERTEX,{"derivedFrom":[subQ0,sQuery(id+"F0.wireOp",EDGE,"E1.1.5.0")]});Q0=makeQuery(id+"F0.imprint","IMPRINT",FACE,{"disambiguationData":[TD([[makeQuery(id+"F0.imprint","IMPRINT",EDGE,{"disambiguationData":[TD([[subQ1,1.0]])],"derivedFrom":subQ0}),1.0]])]});}
            extrude(context, id + "F52", {"entities" : qUnion([Q0]), "depth" : 520 * mm});
        }
        {
            var Q0;
            {var subQ0=sQuery(id+"F0.wireOp",EDGE,"E1.2.4.0");var subQ1=makeQuery(id+"F0.imprint","INTERSECT",VERTEX,{"derivedFrom":[subQ0,sQuery(id+"F0.wireOp",EDGE,"E1.2.5.0")]});Q0=makeQuery(id+"F0.imprint","IMPRINT",FACE,{"disambiguationData":[TD([[makeQuery(id+"F0.imprint","IMPRINT",EDGE,{"disambiguationData":[TD([[subQ1,1.0]])],"derivedFrom":subQ0}),1.0]])]});}
            extrude(context, id + "F53", {"entities" : qUnion([Q0]), "depth" : 530 * mm});
        }
        {
            var Q0;
            {var subQ0=sQuery(id+"F0.wireOp",EDGE,"E1.3.4.0");var subQ1=makeQuery(id+"F0.imprint","INTERSECT",VERTEX,{"derivedFrom":[subQ0,sQuery(id+"F0.wireOp",EDGE,"E1.3.5.0")]});Q0=makeQuery(id+"F0.imprint","IMPRINT",FACE,{"disambiguationData":[TD([[makeQuery(id+"F0.imprint","IMPRINT",EDGE,{"disambiguationData":[TD([[subQ1,1.0]])],"derivedFrom":subQ0}),1.0]])]});}
            extrude(context, id + "F54", {"entities" : qUnion([Q0]), "depth" : 540 * mm});
        }
        {
            var Q0;
            {var subQ0=sQuery(id+"F0.wireOp",EDGE,"E1.4.4.0");var subQ1=makeQuery(id+"F0.imprint","INTERSECT",VERTEX,{"derivedFrom":[subQ0,sQuery(id+"F0.wireOp",EDGE,"E1.4.5.0")]});Q0=makeQuery(id+"F0.imprint","IMPRINT",FACE,{"disambiguationData":[TD([[makeQuery(id+"F0.imprint","IMPRINT",EDGE,{"disambiguationData":[TD([[subQ1,1.0]])],"derivedFrom":subQ0}),1.0]])]});}
            extrude(context, id + "F55", {"entities" : qUnion([Q0]), "depth" : 550 * mm});
        }
        {
            var Q0;
            {var subQ0=sQuery(id+"F0.wireOp",EDGE,"E1.5.4.0");var subQ1=makeQuery(id+"F0.imprint","INTERSECT",VERTEX,{"derivedFrom":[subQ0,sQuery(id+"F0.wireOp",EDGE,"E1.5.5.0")]});Q0=makeQuery(id+"F0.imprint","IMPRINT",FACE,{"disambiguationData":[TD([[makeQuery(id+"F0.imprint","IMPRINT",EDGE,{"disambiguationData":[TD([[subQ1,1.0]])],"derivedFrom":subQ0}),1.0]])]});}
            extrude(context, id + "F56", {"entities" : qUnion([Q0]), "depth" : 560 * mm});
        }
        {
            var Q0;
            {var subQ0=sQuery(id+"F0.wireOp",EDGE,"E1.6.4.0");var subQ1=makeQuery(id+"F0.imprint","INTERSECT",VERTEX,{"derivedFrom":[subQ0,sQuery(id+"F0.wireOp",EDGE,"E1.6.5.0")]});Q0=makeQuery(id+"F0.imprint","IMPRINT",FACE,{"disambiguationData":[TD([[makeQuery(id+"F0.imprint","IMPRINT",EDGE,{"disambiguationData":[TD([[subQ1,1.0]])],"derivedFrom":subQ0}),1.0]])]});}
            extrude(context, id + "F57", {"entities" : qUnion([Q0]), "depth" : 570 * mm});
        }
        {
            var Q0;
            {var subQ0=sQuery(id+"F0.wireOp",EDGE,"E1.7.4.0");var subQ1=makeQuery(id+"F0.imprint","INTERSECT",VERTEX,{"derivedFrom":[subQ0,sQuery(id+"F0.wireOp",EDGE,"E1.7.5.0")]});Q0=makeQuery(id+"F0.imprint","IMPRINT",FACE,{"disambiguationData":[TD([[makeQuery(id+"F0.imprint","IMPRINT",EDGE,{"disambiguationData":[TD([[subQ1,1.0]])],"derivedFrom":subQ0}),1.0]])]});}
            extrude(context, id + "F58", {"entities" : qUnion([Q0]), "depth" : 580 * mm});
        }
        {
            var Q0;
            {var subQ0=sQuery(id+"F0.wireOp",EDGE,"E1.8.4.0");var subQ1=makeQuery(id+"F0.imprint","INTERSECT",VERTEX,{"derivedFrom":[subQ0,sQuery(id+"F0.wireOp",EDGE,"E1.8.5.0")]});Q0=makeQuery(id+"F0.imprint","IMPRINT",FACE,{"disambiguationData":[TD([[makeQuery(id+"F0.imprint","IMPRINT",EDGE,{"disambiguationData":[TD([[subQ1,1.0]])],"derivedFrom":subQ0}),1.0]])]});}
            extrude(context, id + "F59", {"entities" : qUnion([Q0]), "depth" : 590 * mm});
        }
        {
            var Q0;
            {var subQ0=sQuery(id+"F0.wireOp",EDGE,"E1.9.4.0");var subQ1=makeQuery(id+"F0.imprint","INTERSECT",VERTEX,{"derivedFrom":[subQ0,sQuery(id+"F0.wireOp",EDGE,"E1.9.5.0")]});Q0=makeQuery(id+"F0.imprint","IMPRINT",FACE,{"disambiguationData":[TD([[makeQuery(id+"F0.imprint","IMPRINT",EDGE,{"disambiguationData":[TD([[subQ1,-1.0]])],"derivedFrom":subQ0}),1.0]])]});}
            extrude(context, id + "F60", {"entities" : qUnion([Q0]), "depth" : 600 * mm});
        }
        {
            var Q0;
            {var subQ0=sQuery(id+"F0.wireOp",EDGE,"E1.0.3.0");var subQ1=makeQuery(id+"F0.imprint","INTERSECT",VERTEX,{"derivedFrom":[subQ0,sQuery(id+"F0.wireOp",EDGE,"E1.0.4.0")]});Q0=makeQuery(id+"F0.imprint","IMPRINT",FACE,{"disambiguationData":[TD([[makeQuery(id+"F0.imprint","IMPRINT",EDGE,{"disambiguationData":[TD([[subQ1,1.0]])],"derivedFrom":subQ0}),1.0]])]});}
            extrude(context, id + "F61", {"entities" : qUnion([Q0]), "depth" : 610 * mm});
        }
        {
            var Q0;
            {var subQ0=sQuery(id+"F0.wireOp",EDGE,"E1.1.3.0");var subQ1=makeQuery(id+"F0.imprint","INTERSECT",VERTEX,{"derivedFrom":[subQ0,sQuery(id+"F0.wireOp",EDGE,"E1.1.4.0")]});Q0=makeQuery(id+"F0.imprint","IMPRINT",FACE,{"disambiguationData":[TD([[makeQuery(id+"F0.imprint","IMPRINT",EDGE,{"disambiguationData":[TD([[subQ1,1.0]])],"derivedFrom":subQ0}),1.0]])]});}
            extrude(context, id + "F62", {"entities" : qUnion([Q0]), "depth" : 620 * mm});
        }
        {
            var Q0;
            {var subQ0=sQuery(id+"F0.wireOp",EDGE,"E1.2.3.0");var subQ1=makeQuery(id+"F0.imprint","INTERSECT",VERTEX,{"derivedFrom":[subQ0,sQuery(id+"F0.wireOp",EDGE,"E1.2.4.0")]});Q0=makeQuery(id+"F0.imprint","IMPRINT",FACE,{"disambiguationData":[TD([[makeQuery(id+"F0.imprint","IMPRINT",EDGE,{"disambiguationData":[TD([[subQ1,1.0]])],"derivedFrom":subQ0}),1.0]])]});}
            extrude(context, id + "F63", {"entities" : qUnion([Q0]), "depth" : 630 * mm});
        }
        {
            var Q0;
            {var subQ0=sQuery(id+"F0.wireOp",EDGE,"E1.3.3.0");var subQ1=makeQuery(id+"F0.imprint","INTERSECT",VERTEX,{"derivedFrom":[subQ0,sQuery(id+"F0.wireOp",EDGE,"E1.3.4.0")]});Q0=makeQuery(id+"F0.imprint","IMPRINT",FACE,{"disambiguationData":[TD([[makeQuery(id+"F0.imprint","IMPRINT",EDGE,{"disambiguationData":[TD([[subQ1,1.0]])],"derivedFrom":subQ0}),1.0]])]});}
            extrude(context, id + "F64", {"entities" : qUnion([Q0]), "depth" : 640 * mm});
        }
        {
            var Q0;
            {var subQ0=sQuery(id+"F0.wireOp",EDGE,"E1.4.3.0");var subQ1=makeQuery(id+"F0.imprint","INTERSECT",VERTEX,{"derivedFrom":[subQ0,sQuery(id+"F0.wireOp",EDGE,"E1.4.4.0")]});Q0=makeQuery(id+"F0.imprint","IMPRINT",FACE,{"disambiguationData":[TD([[makeQuery(id+"F0.imprint","IMPRINT",EDGE,{"disambiguationData":[TD([[subQ1,1.0]])],"derivedFrom":subQ0}),1.0]])]});}
            extrude(context, id + "F65", {"entities" : qUnion([Q0]), "depth" : 650 * mm});
        }
        {
            var Q0;
            {var subQ0=sQuery(id+"F0.wireOp",EDGE,"E1.5.3.0");var subQ1=makeQuery(id+"F0.imprint","INTERSECT",VERTEX,{"derivedFrom":[subQ0,sQuery(id+"F0.wireOp",EDGE,"E1.5.4.0")]});Q0=makeQuery(id+"F0.imprint","IMPRINT",FACE,{"disambiguationData":[TD([[makeQuery(id+"F0.imprint","IMPRINT",EDGE,{"disambiguationData":[TD([[subQ1,1.0]])],"derivedFrom":subQ0}),1.0]])]});}
            extrude(context, id + "F66", {"entities" : qUnion([Q0]), "depth" : 660 * mm});
        }
        {
            var Q0;
            {var subQ0=sQuery(id+"F0.wireOp",EDGE,"E1.6.3.0");var subQ1=makeQuery(id+"F0.imprint","INTERSECT",VERTEX,{"derivedFrom":[subQ0,sQuery(id+"F0.wireOp",EDGE,"E1.6.4.0")]});Q0=makeQuery(id+"F0.imprint","IMPRINT",FACE,{"disambiguationData":[TD([[makeQuery(id+"F0.imprint","IMPRINT",EDGE,{"disambiguationData":[TD([[subQ1,1.0]])],"derivedFrom":subQ0}),1.0]])]});}
            extrude(context, id + "F67", {"entities" : qUnion([Q0]), "depth" : 670 * mm});
        }
        {
            var Q0;
            {var subQ0=sQuery(id+"F0.wireOp",EDGE,"E1.7.3.0");var subQ1=makeQuery(id+"F0.imprint","INTERSECT",VERTEX,{"derivedFrom":[subQ0,sQuery(id+"F0.wireOp",EDGE,"E1.7.4.0")]});Q0=makeQuery(id+"F0.imprint","IMPRINT",FACE,{"disambiguationData":[TD([[makeQuery(id+"F0.imprint","IMPRINT",EDGE,{"disambiguationData":[TD([[subQ1,1.0]])],"derivedFrom":subQ0}),1.0]])]});}
            extrude(context, id + "F68", {"entities" : qUnion([Q0]), "depth" : 680 * mm});
        }
        {
            var Q0;
            {var subQ0=sQuery(id+"F0.wireOp",EDGE,"E1.8.3.0");var subQ1=makeQuery(id+"F0.imprint","INTERSECT",VERTEX,{"derivedFrom":[subQ0,sQuery(id+"F0.wireOp",EDGE,"E1.8.4.0")]});Q0=makeQuery(id+"F0.imprint","IMPRINT",FACE,{"disambiguationData":[TD([[makeQuery(id+"F0.imprint","IMPRINT",EDGE,{"disambiguationData":[TD([[subQ1,1.0]])],"derivedFrom":subQ0}),1.0]])]});}
            extrude(context, id + "F69", {"entities" : qUnion([Q0]), "depth" : 690 * mm});
        }
        {
            var Q0;
            {var subQ0=sQuery(id+"F0.wireOp",EDGE,"E1.9.3.0");var subQ1=makeQuery(id+"F0.imprint","INTERSECT",VERTEX,{"derivedFrom":[subQ0,sQuery(id+"F0.wireOp",EDGE,"E1.9.4.0")]});Q0=makeQuery(id+"F0.imprint","IMPRINT",FACE,{"disambiguationData":[TD([[makeQuery(id+"F0.imprint","IMPRINT",EDGE,{"disambiguationData":[TD([[subQ1,-1.0]])],"derivedFrom":subQ0}),1.0]])]});}
            extrude(context, id + "F70", {"entities" : qUnion([Q0]), "depth" : 700 * mm});
        }
        {
            var Q0;
            {var subQ0=sQuery(id+"F0.wireOp",EDGE,"E1.0.2.0");var subQ1=makeQuery(id+"F0.imprint","INTERSECT",VERTEX,{"derivedFrom":[subQ0,sQuery(id+"F0.wireOp",EDGE,"E1.0.3.0")]});Q0=makeQuery(id+"F0.imprint","IMPRINT",FACE,{"disambiguationData":[TD([[makeQuery(id+"F0.imprint","IMPRINT",EDGE,{"disambiguationData":[TD([[subQ1,1.0]])],"derivedFrom":subQ0}),1.0]])]});}
            extrude(context, id + "F71", {"entities" : qUnion([Q0]), "depth" : 710 * mm});
        }
        {
            var Q0;
            {var subQ0=sQuery(id+"F0.wireOp",EDGE,"E1.1.2.0");var subQ1=makeQuery(id+"F0.imprint","INTERSECT",VERTEX,{"derivedFrom":[subQ0,sQuery(id+"F0.wireOp",EDGE,"E1.1.3.0")]});Q0=makeQuery(id+"F0.imprint","IMPRINT",FACE,{"disambiguationData":[TD([[makeQuery(id+"F0.imprint","IMPRINT",EDGE,{"disambiguationData":[TD([[subQ1,1.0]])],"derivedFrom":subQ0}),1.0]])]});}
            extrude(context, id + "F72", {"entities" : qUnion([Q0]), "depth" : 720 * mm});
        }
        {
            var Q0;
            {var subQ0=sQuery(id+"F0.wireOp",EDGE,"E1.2.2.0");var subQ1=makeQuery(id+"F0.imprint","INTERSECT",VERTEX,{"derivedFrom":[subQ0,sQuery(id+"F0.wireOp",EDGE,"E1.2.3.0")]});Q0=makeQuery(id+"F0.imprint","IMPRINT",FACE,{"disambiguationData":[TD([[makeQuery(id+"F0.imprint","IMPRINT",EDGE,{"disambiguationData":[TD([[subQ1,1.0]])],"derivedFrom":subQ0}),1.0]])]});}
            extrude(context, id + "F73", {"entities" : qUnion([Q0]), "depth" : 730 * mm});
        }
        {
            var Q0;
            {var subQ0=sQuery(id+"F0.wireOp",EDGE,"E1.3.2.0");var subQ1=makeQuery(id+"F0.imprint","INTERSECT",VERTEX,{"derivedFrom":[subQ0,sQuery(id+"F0.wireOp",EDGE,"E1.3.3.0")]});Q0=makeQuery(id+"F0.imprint","IMPRINT",FACE,{"disambiguationData":[TD([[makeQuery(id+"F0.imprint","IMPRINT",EDGE,{"disambiguationData":[TD([[subQ1,1.0]])],"derivedFrom":subQ0}),1.0]])]});}
            extrude(context, id + "F74", {"entities" : qUnion([Q0]), "depth" : 740 * mm});
        }
        {
            var Q0;
            {var subQ0=sQuery(id+"F0.wireOp",EDGE,"E1.4.2.0");var subQ1=makeQuery(id+"F0.imprint","INTERSECT",VERTEX,{"derivedFrom":[subQ0,sQuery(id+"F0.wireOp",EDGE,"E1.4.3.0")]});Q0=makeQuery(id+"F0.imprint","IMPRINT",FACE,{"disambiguationData":[TD([[makeQuery(id+"F0.imprint","IMPRINT",EDGE,{"disambiguationData":[TD([[subQ1,1.0]])],"derivedFrom":subQ0}),1.0]])]});}
            extrude(context, id + "F75", {"entities" : qUnion([Q0]), "depth" : 750 * mm});
        }
        {
            var Q0;
            {var subQ0=sQuery(id+"F0.wireOp",EDGE,"E1.5.2.0");var subQ1=makeQuery(id+"F0.imprint","INTERSECT",VERTEX,{"derivedFrom":[subQ0,sQuery(id+"F0.wireOp",EDGE,"E1.5.3.0")]});Q0=makeQuery(id+"F0.imprint","IMPRINT",FACE,{"disambiguationData":[TD([[makeQuery(id+"F0.imprint","IMPRINT",EDGE,{"disambiguationData":[TD([[subQ1,1.0]])],"derivedFrom":subQ0}),1.0]])]});}
            extrude(context, id + "F76", {"entities" : qUnion([Q0]), "depth" : 760 * mm});
        }
        {
            var Q0;
            {var subQ0=sQuery(id+"F0.wireOp",EDGE,"E1.6.2.0");var subQ1=makeQuery(id+"F0.imprint","INTERSECT",VERTEX,{"derivedFrom":[subQ0,sQuery(id+"F0.wireOp",EDGE,"E1.6.3.0")]});Q0=makeQuery(id+"F0.imprint","IMPRINT",FACE,{"disambiguationData":[TD([[makeQuery(id+"F0.imprint","IMPRINT",EDGE,{"disambiguationData":[TD([[subQ1,1.0]])],"derivedFrom":subQ0}),1.0]])]});}
            extrude(context, id + "F77", {"entities" : qUnion([Q0]), "depth" : 770 * mm});
        }
        {
            var Q0;
            {var subQ0=sQuery(id+"F0.wireOp",EDGE,"E1.7.2.0");var subQ1=makeQuery(id+"F0.imprint","INTERSECT",VERTEX,{"derivedFrom":[subQ0,sQuery(id+"F0.wireOp",EDGE,"E1.7.3.0")]});Q0=makeQuery(id+"F0.imprint","IMPRINT",FACE,{"disambiguationData":[TD([[makeQuery(id+"F0.imprint","IMPRINT",EDGE,{"disambiguationData":[TD([[subQ1,1.0]])],"derivedFrom":subQ0}),1.0]])]});}
            extrude(context, id + "F78", {"entities" : qUnion([Q0]), "depth" : 780 * mm});
        }
        {
            var Q0;
            {var subQ0=sQuery(id+"F0.wireOp",EDGE,"E1.8.2.0");var subQ1=makeQuery(id+"F0.imprint","INTERSECT",VERTEX,{"derivedFrom":[subQ0,sQuery(id+"F0.wireOp",EDGE,"E1.8.3.0")]});Q0=makeQuery(id+"F0.imprint","IMPRINT",FACE,{"disambiguationData":[TD([[makeQuery(id+"F0.imprint","IMPRINT",EDGE,{"disambiguationData":[TD([[subQ1,1.0]])],"derivedFrom":subQ0}),1.0]])]});}
            extrude(context, id + "F79", {"entities" : qUnion([Q0]), "depth" : 790 * mm});
        }
        {
            var Q0;
            {var subQ0=sQuery(id+"F0.wireOp",EDGE,"E1.9.2.0");var subQ1=makeQuery(id+"F0.imprint","INTERSECT",VERTEX,{"derivedFrom":[subQ0,sQuery(id+"F0.wireOp",EDGE,"E1.9.3.0")]});Q0=makeQuery(id+"F0.imprint","IMPRINT",FACE,{"disambiguationData":[TD([[makeQuery(id+"F0.imprint","IMPRINT",EDGE,{"disambiguationData":[TD([[subQ1,-1.0]])],"derivedFrom":subQ0}),1.0]])]});}
            extrude(context, id + "F80", {"entities" : qUnion([Q0]), "depth" : 800 * mm});
        }
        {
            var Q0;
            {var subQ0=sQuery(id+"F0.wireOp",EDGE,"E1.0.1.0");var subQ1=makeQuery(id+"F0.imprint","INTERSECT",VERTEX,{"derivedFrom":[subQ0,sQuery(id+"F0.wireOp",EDGE,"E1.0.2.0")]});Q0=makeQuery(id+"F0.imprint","IMPRINT",FACE,{"disambiguationData":[TD([[makeQuery(id+"F0.imprint","IMPRINT",EDGE,{"disambiguationData":[TD([[subQ1,1.0]])],"derivedFrom":subQ0}),1.0]])]});}
            extrude(context, id + "F81", {"entities" : qUnion([Q0]), "depth" : 810 * mm});
        }
        {
            var Q0;
            {var subQ0=sQuery(id+"F0.wireOp",EDGE,"E1.1.1.0");var subQ1=makeQuery(id+"F0.imprint","INTERSECT",VERTEX,{"derivedFrom":[subQ0,sQuery(id+"F0.wireOp",EDGE,"E1.1.2.0")]});Q0=makeQuery(id+"F0.imprint","IMPRINT",FACE,{"disambiguationData":[TD([[makeQuery(id+"F0.imprint","IMPRINT",EDGE,{"disambiguationData":[TD([[subQ1,1.0]])],"derivedFrom":subQ0}),1.0]])]});}
            extrude(context, id + "F82", {"entities" : qUnion([Q0]), "depth" : 820 * mm});
        }
        {
            var Q0;
            {var subQ0=sQuery(id+"F0.wireOp",EDGE,"E1.2.1.0");var subQ1=makeQuery(id+"F0.imprint","INTERSECT",VERTEX,{"derivedFrom":[subQ0,sQuery(id+"F0.wireOp",EDGE,"E1.2.2.0")]});Q0=makeQuery(id+"F0.imprint","IMPRINT",FACE,{"disambiguationData":[TD([[makeQuery(id+"F0.imprint","IMPRINT",EDGE,{"disambiguationData":[TD([[subQ1,1.0]])],"derivedFrom":subQ0}),1.0]])]});}
            extrude(context, id + "F83", {"entities" : qUnion([Q0]), "depth" : 830 * mm});
        }
        {
            var Q0;
            {var subQ0=sQuery(id+"F0.wireOp",EDGE,"E1.3.1.0");var subQ1=makeQuery(id+"F0.imprint","INTERSECT",VERTEX,{"derivedFrom":[subQ0,sQuery(id+"F0.wireOp",EDGE,"E1.3.2.0")]});Q0=makeQuery(id+"F0.imprint","IMPRINT",FACE,{"disambiguationData":[TD([[makeQuery(id+"F0.imprint","IMPRINT",EDGE,{"disambiguationData":[TD([[subQ1,1.0]])],"derivedFrom":subQ0}),1.0]])]});}
            extrude(context, id + "F84", {"entities" : qUnion([Q0]), "depth" : 840 * mm});
        }
        {
            var Q0;
            {var subQ0=sQuery(id+"F0.wireOp",EDGE,"E1.4.1.0");var subQ1=makeQuery(id+"F0.imprint","INTERSECT",VERTEX,{"derivedFrom":[subQ0,sQuery(id+"F0.wireOp",EDGE,"E1.4.2.0")]});Q0=makeQuery(id+"F0.imprint","IMPRINT",FACE,{"disambiguationData":[TD([[makeQuery(id+"F0.imprint","IMPRINT",EDGE,{"disambiguationData":[TD([[subQ1,1.0]])],"derivedFrom":subQ0}),1.0]])]});}
            extrude(context, id + "F85", {"entities" : qUnion([Q0]), "depth" : 850 * mm});
        }
        {
            var Q0;
            {var subQ0=sQuery(id+"F0.wireOp",EDGE,"E1.5.1.0");var subQ1=makeQuery(id+"F0.imprint","INTERSECT",VERTEX,{"derivedFrom":[subQ0,sQuery(id+"F0.wireOp",EDGE,"E1.5.2.0")]});Q0=makeQuery(id+"F0.imprint","IMPRINT",FACE,{"disambiguationData":[TD([[makeQuery(id+"F0.imprint","IMPRINT",EDGE,{"disambiguationData":[TD([[subQ1,1.0]])],"derivedFrom":subQ0}),1.0]])]});}
            extrude(context, id + "F86", {"entities" : qUnion([Q0]), "depth" : 860 * mm});
        }
        {
            var Q0;
            {var subQ0=sQuery(id+"F0.wireOp",EDGE,"E1.6.1.0");var subQ1=makeQuery(id+"F0.imprint","INTERSECT",VERTEX,{"derivedFrom":[subQ0,sQuery(id+"F0.wireOp",EDGE,"E1.6.2.0")]});Q0=makeQuery(id+"F0.imprint","IMPRINT",FACE,{"disambiguationData":[TD([[makeQuery(id+"F0.imprint","IMPRINT",EDGE,{"disambiguationData":[TD([[subQ1,1.0]])],"derivedFrom":subQ0}),1.0]])]});}
            extrude(context, id + "F87", {"entities" : qUnion([Q0]), "depth" : 870 * mm});
        }
        {
            var Q0;
            {var subQ0=sQuery(id+"F0.wireOp",EDGE,"E1.7.1.0");var subQ1=makeQuery(id+"F0.imprint","INTERSECT",VERTEX,{"derivedFrom":[subQ0,sQuery(id+"F0.wireOp",EDGE,"E1.7.2.0")]});Q0=makeQuery(id+"F0.imprint","IMPRINT",FACE,{"disambiguationData":[TD([[makeQuery(id+"F0.imprint","IMPRINT",EDGE,{"disambiguationData":[TD([[subQ1,1.0]])],"derivedFrom":subQ0}),1.0]])]});}
            extrude(context, id + "F88", {"entities" : qUnion([Q0]), "depth" : 880 * mm});
        }
        {
            var Q0;
            {var subQ0=sQuery(id+"F0.wireOp",EDGE,"E1.8.1.0");var subQ1=makeQuery(id+"F0.imprint","INTERSECT",VERTEX,{"derivedFrom":[subQ0,sQuery(id+"F0.wireOp",EDGE,"E1.8.2.0")]});Q0=makeQuery(id+"F0.imprint","IMPRINT",FACE,{"disambiguationData":[TD([[makeQuery(id+"F0.imprint","IMPRINT",EDGE,{"disambiguationData":[TD([[subQ1,1.0]])],"derivedFrom":subQ0}),1.0]])]});}
            extrude(context, id + "F89", {"entities" : qUnion([Q0]), "depth" : 890 * mm});
        }
        {
            var Q0;
            {var subQ0=sQuery(id+"F0.wireOp",EDGE,"E1.9.1.0");var subQ1=makeQuery(id+"F0.imprint","INTERSECT",VERTEX,{"derivedFrom":[subQ0,sQuery(id+"F0.wireOp",EDGE,"E1.9.2.0")]});Q0=makeQuery(id+"F0.imprint","IMPRINT",FACE,{"disambiguationData":[TD([[makeQuery(id+"F0.imprint","IMPRINT",EDGE,{"disambiguationData":[TD([[subQ1,-1.0]])],"derivedFrom":subQ0}),1.0]])]});}
            extrude(context, id + "F90", {"entities" : qUnion([Q0]), "depth" : 900 * mm});
        }
        {
            var Q0;
            {var subQ0=sQuery(id+"F0.wireOp",EDGE,"E0");var subQ1=makeQuery(id+"F0.imprint","INTERSECT",VERTEX,{"derivedFrom":[subQ0,sQuery(id+"F0.wireOp",EDGE,"E1.0.1.0")]});Q0=makeQuery(id+"F0.imprint","IMPRINT",FACE,{"disambiguationData":[TD([[makeQuery(id+"F0.imprint","IMPRINT",EDGE,{"disambiguationData":[TD([[subQ1,1.0]])],"derivedFrom":subQ0}),1.0]])]});}
            extrude(context, id + "F91", {"entities" : qUnion([Q0]), "depth" : 910 * mm});
        }
        {
            var Q0;
            {var subQ0=sQuery(id+"F0.wireOp",EDGE,"E1.1.0.0");var subQ1=makeQuery(id+"F0.imprint","INTERSECT",VERTEX,{"derivedFrom":[subQ0,sQuery(id+"F0.wireOp",EDGE,"E1.2.0.0")]});Q0=makeQuery(id+"F0.imprint","IMPRINT",FACE,{"disambiguationData":[TD([[makeQuery(id+"F0.imprint","IMPRINT",EDGE,{"disambiguationData":[TD([[subQ1,-1.0]])],"derivedFrom":subQ0}),1.0]])]});}
            extrude(context, id + "F92", {"entities" : qUnion([Q0]), "depth" : 920 * mm});
        }
        {
            var Q0;
            {var subQ0=sQuery(id+"F0.wireOp",EDGE,"E1.2.0.0");var subQ1=makeQuery(id+"F0.imprint","INTERSECT",VERTEX,{"derivedFrom":[subQ0,sQuery(id+"F0.wireOp",EDGE,"E1.3.0.0")]});Q0=makeQuery(id+"F0.imprint","IMPRINT",FACE,{"disambiguationData":[TD([[makeQuery(id+"F0.imprint","IMPRINT",EDGE,{"disambiguationData":[TD([[subQ1,-1.0]])],"derivedFrom":subQ0}),1.0]])]});}
            extrude(context, id + "F93", {"entities" : qUnion([Q0]), "depth" : 930 * mm});
        }
        {
            var Q0;
            {var subQ0=sQuery(id+"F0.wireOp",EDGE,"E1.3.0.0");var subQ1=makeQuery(id+"F0.imprint","INTERSECT",VERTEX,{"derivedFrom":[subQ0,sQuery(id+"F0.wireOp",EDGE,"E1.4.0.0")]});Q0=makeQuery(id+"F0.imprint","IMPRINT",FACE,{"disambiguationData":[TD([[makeQuery(id+"F0.imprint","IMPRINT",EDGE,{"disambiguationData":[TD([[subQ1,-1.0]])],"derivedFrom":subQ0}),1.0]])]});}
            extrude(context, id + "F94", {"entities" : qUnion([Q0]), "depth" : 940 * mm});
        }
        {
            var Q0;
            {var subQ0=sQuery(id+"F0.wireOp",EDGE,"E1.4.0.0");var subQ1=makeQuery(id+"F0.imprint","INTERSECT",VERTEX,{"derivedFrom":[subQ0,sQuery(id+"F0.wireOp",EDGE,"E1.5.0.0")]});Q0=makeQuery(id+"F0.imprint","IMPRINT",FACE,{"disambiguationData":[TD([[makeQuery(id+"F0.imprint","IMPRINT",EDGE,{"disambiguationData":[TD([[subQ1,-1.0]])],"derivedFrom":subQ0}),1.0]])]});}
            extrude(context, id + "F95", {"entities" : qUnion([Q0]), "depth" : 950 * mm});
        }
        {
            var Q0;
            {var subQ0=sQuery(id+"F0.wireOp",EDGE,"E1.5.0.0");var subQ1=makeQuery(id+"F0.imprint","INTERSECT",VERTEX,{"derivedFrom":[subQ0,sQuery(id+"F0.wireOp",EDGE,"E1.6.0.0")]});Q0=makeQuery(id+"F0.imprint","IMPRINT",FACE,{"disambiguationData":[TD([[makeQuery(id+"F0.imprint","IMPRINT",EDGE,{"disambiguationData":[TD([[subQ1,-1.0]])],"derivedFrom":subQ0}),1.0]])]});}
            extrude(context, id + "F96", {"entities" : qUnion([Q0]), "depth" : 960 * mm});
        }
        {
            var Q0;
            {var subQ0=sQuery(id+"F0.wireOp",EDGE,"E1.6.0.0");var subQ1=makeQuery(id+"F0.imprint","INTERSECT",VERTEX,{"derivedFrom":[subQ0,sQuery(id+"F0.wireOp",EDGE,"E1.7.0.0")]});Q0=makeQuery(id+"F0.imprint","IMPRINT",FACE,{"disambiguationData":[TD([[makeQuery(id+"F0.imprint","IMPRINT",EDGE,{"disambiguationData":[TD([[subQ1,-1.0]])],"derivedFrom":subQ0}),1.0]])]});}
            extrude(context, id + "F97", {"entities" : qUnion([Q0]), "depth" : 970 * mm});
        }
        {
            var Q0;
            {var subQ0=sQuery(id+"F0.wireOp",EDGE,"E1.7.0.0");var subQ1=makeQuery(id+"F0.imprint","INTERSECT",VERTEX,{"derivedFrom":[subQ0,sQuery(id+"F0.wireOp",EDGE,"E1.8.0.0")]});Q0=makeQuery(id+"F0.imprint","IMPRINT",FACE,{"disambiguationData":[TD([[makeQuery(id+"F0.imprint","IMPRINT",EDGE,{"disambiguationData":[TD([[subQ1,-1.0]])],"derivedFrom":subQ0}),1.0]])]});}
            extrude(context, id + "F98", {"entities" : qUnion([Q0]), "depth" : 980 * mm});
        }
        {
            var Q0;
            {var subQ0=sQuery(id+"F0.wireOp",EDGE,"E1.8.0.0");var subQ1=makeQuery(id+"F0.imprint","INTERSECT",VERTEX,{"derivedFrom":[subQ0,sQuery(id+"F0.wireOp",EDGE,"E1.9.0.0")]});Q0=makeQuery(id+"F0.imprint","IMPRINT",FACE,{"disambiguationData":[TD([[makeQuery(id+"F0.imprint","IMPRINT",EDGE,{"disambiguationData":[TD([[subQ1,-1.0]])],"derivedFrom":subQ0}),1.0]])]});}
            extrude(context, id + "F99", {"entities" : qUnion([Q0]), "depth" : 990 * mm});
        }
        {
            var Q0;
            {var subQ0=sQuery(id+"F0.wireOp",EDGE,"E1.9.0.0");var subQ1=makeQuery(id+"F0.imprint","INTERSECT",VERTEX,{"derivedFrom":[sQuery(id+"F0.wireOp",EDGE,"E1.8.0.0"),subQ0]});Q0=makeQuery(id+"F0.imprint","IMPRINT",FACE,{"disambiguationData":[TD([[makeQuery(id+"F0.imprint","IMPRINT",EDGE,{"disambiguationData":[TD([[subQ1,1.0]])],"derivedFrom":subQ0}),1.0]])]});}
            extrude(context, id + "F100", {"entities" : qUnion([Q0]), "depth" : 1000 * mm});
        }
    });
